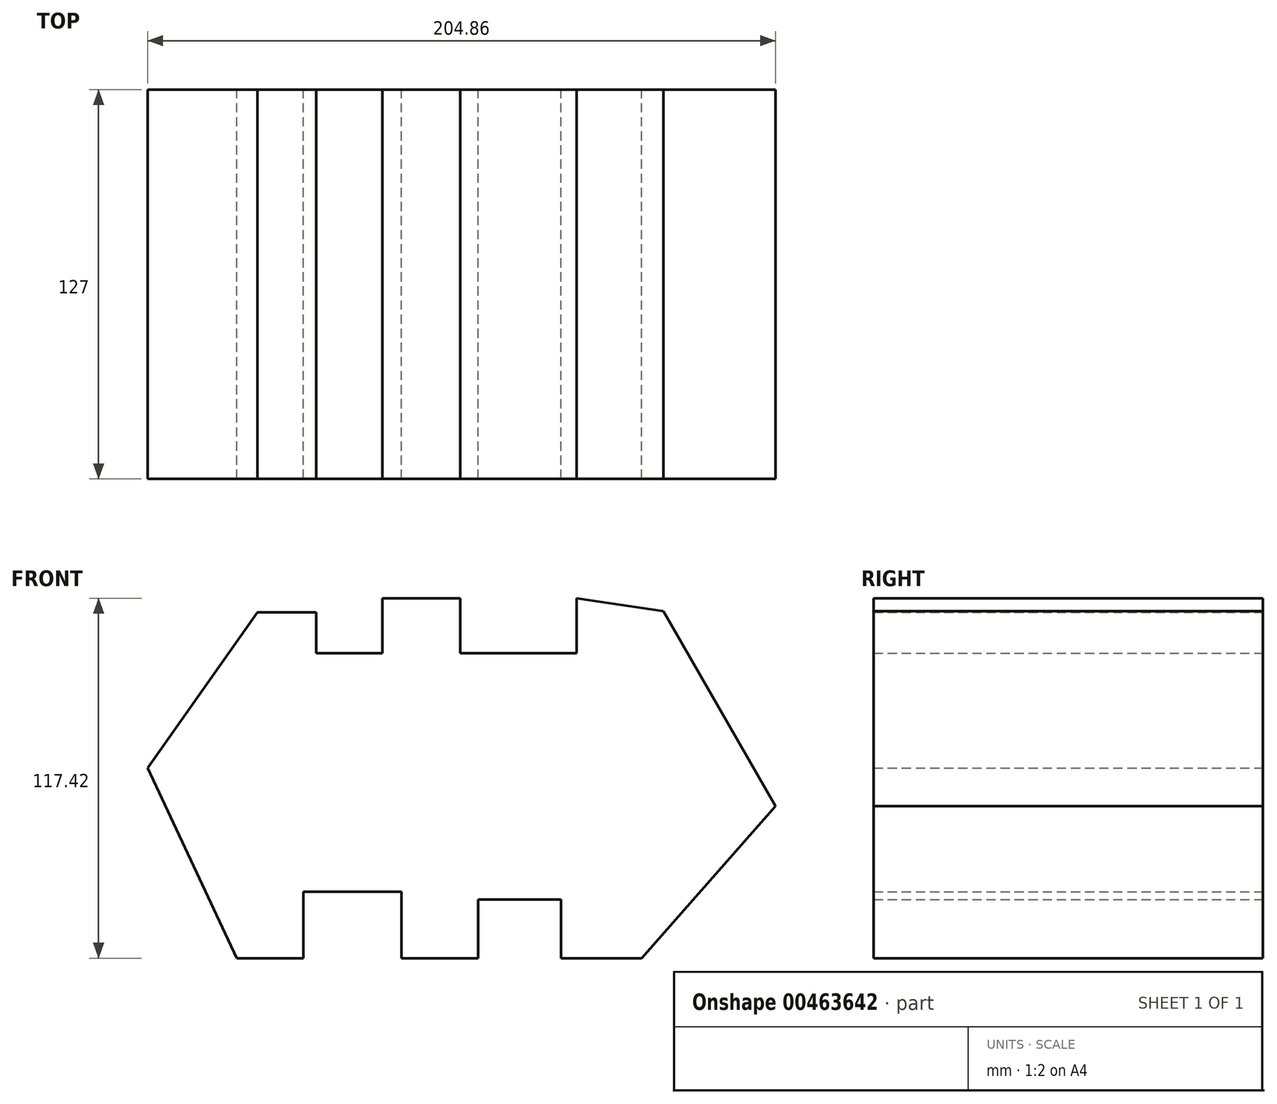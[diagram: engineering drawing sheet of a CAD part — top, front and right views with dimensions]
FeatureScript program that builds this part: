
annotation { "Feature Type Name" : "Feature", "Feature Type Description" : "" }
export const myFeature = defineFeature(function(context is Context, id is Id, definition is map)
    precondition{}
    {
        {
            var Q0;
            Q0=qCreatedBy(makeId("Front.planeOp"),FACE);
            var sketch = newSketch(context, id + "F0", { "sketchPlane" : qUnion([Q0])});
            skLineSegment(sketch, "E0", {"start": v(-18.74, 36.95) * mm, "end": v(17.9, -26.75) * mm});
            skLineSegment(sketch, "E1", {"start": v(17.9, -26.75) * mm, "end": v(-25.82, -76.3) * mm});
            skLineSegment(sketch, "E2", {"start": v(-25.82, -76.3) * mm, "end": v(-52.05, -76.3) * mm});
            skLineSegment(sketch, "E3", {"start": v(-52.05, -76.3) * mm, "end": v(-52.05, -57.15) * mm});
            skLineSegment(sketch, "E4", {"start": v(-52.05, -57.15) * mm, "end": v(-79.11, -57.15) * mm});
            skLineSegment(sketch, "E5", {"start": v(-79.11, -57.15) * mm, "end": v(-79.11, -76.3) * mm});
            skLineSegment(sketch, "E6", {"start": v(-79.11, -76.3) * mm, "end": v(-104.1, -76.3) * mm});
            skLineSegment(sketch, "E7", {"start": v(-104.1, -76.3) * mm, "end": v(-104.1, -54.65) * mm});
            skLineSegment(sketch, "E8", {"start": v(-104.1, -54.65) * mm, "end": v(-136.16, -54.65) * mm});
            skLineSegment(sketch, "E9", {"start": v(-136.16, -54.65) * mm, "end": v(-136.16, -76.3) * mm});
            skLineSegment(sketch, "E10", {"start": v(-136.16, -76.3) * mm, "end": v(-157.81, -76.3) * mm});
            skLineSegment(sketch, "E11", {"start": v(-157.81, -76.3) * mm, "end": v(-186.96, -14.26) * mm});
            skLineSegment(sketch, "E12", {"start": v(-186.96, -14.26) * mm, "end": v(-151.15, 36.54) * mm});
            skLineSegment(sketch, "E13", {"start": v(-151.15, 36.54) * mm, "end": v(-132, 36.54) * mm});
            skLineSegment(sketch, "E14", {"start": v(-132, 36.54) * mm, "end": v(-132, 23.21) * mm});
            skLineSegment(sketch, "E15", {"start": v(-132, 23.21) * mm, "end": v(-110.34, 23.21) * mm});
            skLineSegment(sketch, "E16", {"start": v(-110.34, 23.21) * mm, "end": v(-110.34, 41.12) * mm});
            skLineSegment(sketch, "E17", {"start": v(-110.34, 41.12) * mm, "end": v(-84.94, 41.12) * mm});
            skLineSegment(sketch, "E18", {"start": v(-84.94, 41.12) * mm, "end": v(-84.94, 23.21) * mm});
            skLineSegment(sketch, "E19", {"start": v(-84.94, 23.21) * mm, "end": v(-47.05, 23.21) * mm});
            skLineSegment(sketch, "E20", {"start": v(-47.05, 23.21) * mm, "end": v(-47.05, 41.12) * mm});
            skLineSegment(sketch, "E21", {"start": v(-47.05, 41.12) * mm, "end": v(-18.74, 36.95) * mm});
            skSolve(sketch);
        }
        {
            var Q0;
            Q0 = qSketchRegion(id + "F0", true);
            extrude(context, id + "F1", {"entities" : qUnion([Q0]), "depth" : 127 * mm});
        }
    });
